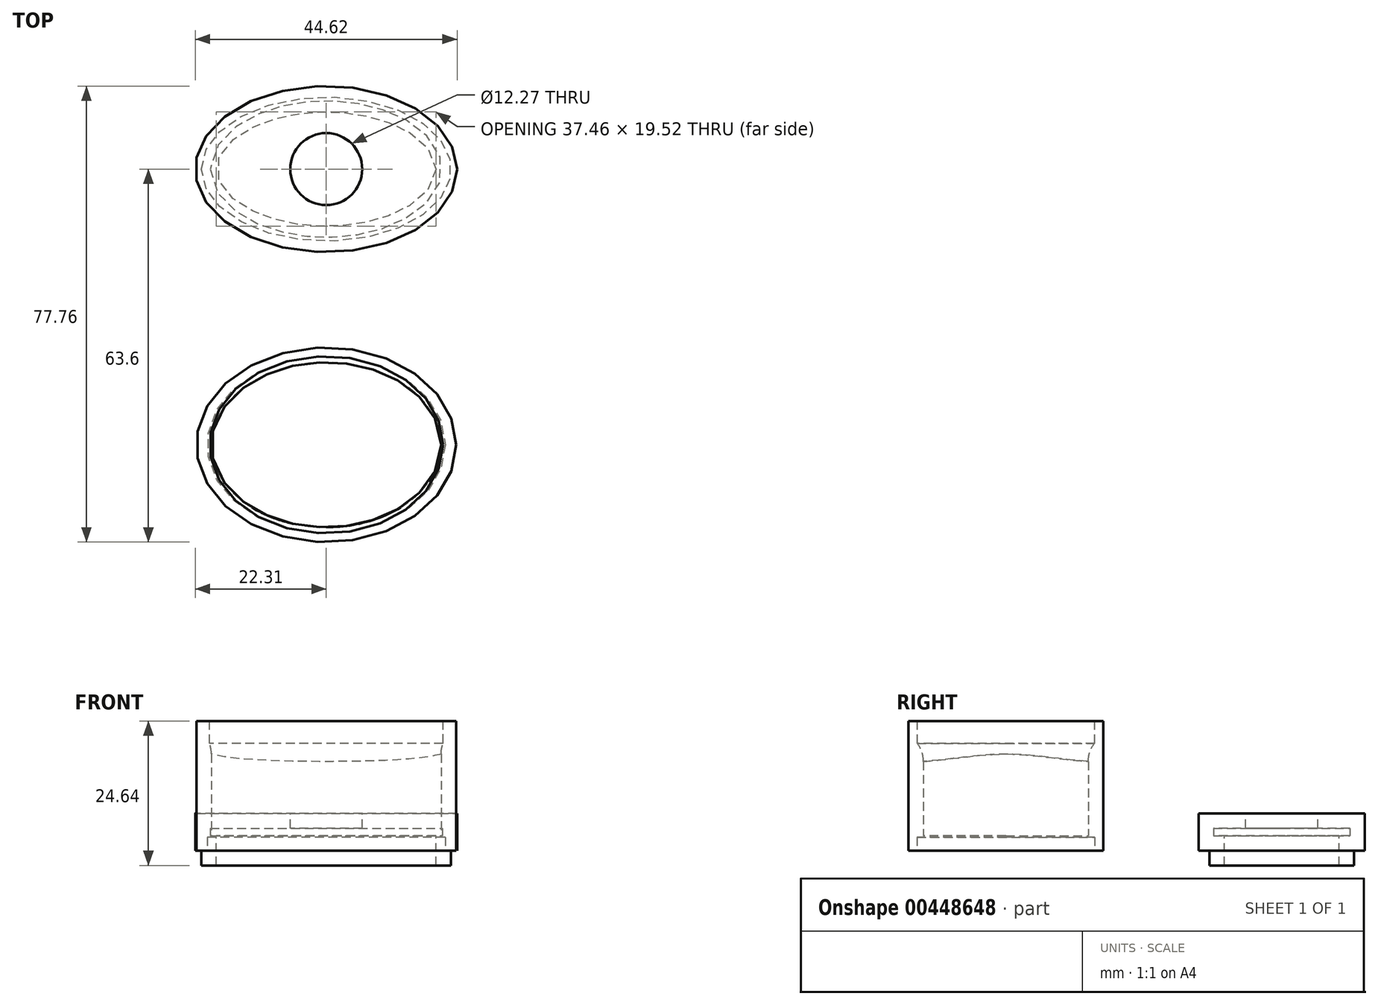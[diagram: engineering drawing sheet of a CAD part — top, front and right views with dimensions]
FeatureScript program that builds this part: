
annotation { "Feature Type Name" : "Feature", "Feature Type Description" : "" }
export const myFeature = defineFeature(function(context is Context, id is Id, definition is map)
    precondition{}
    {
        {
            var Q0;
            Q0=qCreatedBy(makeId("Top.planeOp"),FACE);
            var sketch = newSketch(context, id + "F0", { "sketchPlane" : qUnion([Q0])});
            skEllipse(sketch, "E0", {"center": v(0, 0) * mm, "majorRadius": 22.12 * mm, "minorRadius": 16.6 * mm, "majorAxis": v(1, 0)});
            skEllipse(sketch, "E1", {"center": v(0, 51.44) * mm, "majorRadius": 23.6 * mm, "minorRadius": 16.29 * mm, "majorAxis": v(1, 0)});
            skSolve(sketch);
        }
        {
            var Q0;
            Q0=makeQuery(id+"F0.imprint","IMPRINT",FACE,{"disambiguationData":[TD([[makeQuery(id+"F0.imprint","IMPRINT",EDGE,{"derivedFrom":sQuery(id+"F0.wireOp",EDGE,"E0")}),1.0]])]});
            extrude(context, id + "F1", {"entities" : qUnion([Q0]), "depth" : 22.1 * mm});
        }
        {
            var Q0;
            Q0=makeQuery(id+"F1.opExtrude","CAP_FACE",FACE,{"disambiguationData":[OSD([sQuery(id+"F0.wireOp",EDGE,"E0")])],"isStart":false});
            var sketch = newSketch(context, id + "F2", { "sketchPlane" : qUnion([Q0])});
            skEllipse(sketch, "E2", {"center": v(0, 0) * mm, "majorRadius": 19.92 * mm, "minorRadius": 15.11 * mm, "majorAxis": v(1, 0)});
            skSolve(sketch);
        }
        {
            var Q0;
            Q0 = qSketchRegion(id + "F2", true);
            extrude(context, id + "F3", {"entities" : qUnion([Q0]), "operationType" : NewBodyOperationType.REMOVE, "oppositeDirection" : true, "depth" : 3.8 * mm});
        }
        {
            var Q0;
            Q0=makeQuery(id+"F3.boolean.opBoolean","COPY",FACE,{"derivedFrom":makeQuery(id+"F3.opExtrude","CAP_FACE",FACE,{"disambiguationData":[OSD([sQuery(id+"F2.wireOp",EDGE,"E2")])],"isStart":false})});
            shell(context, id + "F4", {"entities" : qUnion([Q0]), "thickness" : 2.54 * mm});
        }
        {
            var Q0;
            Q0=makeQuery(id+"F3.boolean.opBoolean","COPY",EDGE,{"derivedFrom":makeQuery(id+"F3.opExtrude","CAP_EDGE",EDGE,{"disambiguationData":[OSD([sQuery(id+"F2.wireOp",EDGE,"E2")])],"isStart":true})});
            var Q1;
            Q1=makeQuery(id+"F4.opShell","TWEAK_EDGE",EDGE,{"derivedFrom":[makeQuery(id+"F1.opExtrude","SWEPT_FACE",FACE,{"disambiguationData":[OSD([sQuery(id+"F0.wireOp",EDGE,"E0")])]}),makeQuery(id+"F3.boolean.opBoolean","COPY",FACE,{"derivedFrom":makeQuery(id+"F3.opExtrude","CAP_FACE",FACE,{"disambiguationData":[OSD([sQuery(id+"F2.wireOp",EDGE,"E2")])],"isStart":false})})]});
            fillet(context, id + "F5", {"entities" : qUnion([Q0, Q1]), "radius" : 5.08 * mm, "tangentPropagation" : true, "allowEdgeOverflow" : false});
        }
        {
            var Q0;
            Q0=makeQuery(id+"F1.opExtrude","CAP_FACE",FACE,{"disambiguationData":[OSD([sQuery(id+"F0.wireOp",EDGE,"E0")])],"isStart":true});
            var sketch = newSketch(context, id + "F6", { "sketchPlane" : qUnion([Q0])});
            skEllipse(sketch, "E3", {"center": v(0, 0) * mm, "majorRadius": 20.28 * mm, "minorRadius": 15.13 * mm, "majorAxis": v(1, 0)});
            skSolve(sketch);
        }
        {
            var Q0;
            Q0 = qSketchRegion(id + "F6", true);
            extrude(context, id + "F7", {"entities" : qUnion([Q0]), "operationType" : NewBodyOperationType.REMOVE, "oppositeDirection" : true, "depth" : 2.3 * mm});
        }
        {
            var Q0;
            Q0=qCreatedBy(makeId("Top.planeOp"),FACE);
            var sketch = newSketch(context, id + "F8", { "sketchPlane" : qUnion([Q0])});
            skEllipse(sketch, "E4", {"center": v(0, 47.01) * mm, "majorRadius": 22.3 * mm, "minorRadius": 14.16 * mm, "majorAxis": v(1, 0)});
            skSolve(sketch);
        }
        {
            var Q0;
            Q0 = qSketchRegion(id + "F8", true);
            extrude(context, id + "F9", {"entities" : qUnion([Q0]), "depth" : 6.35 * mm});
        }
        {
            var Q0;
            Q0=makeQuery(id+"F9.opExtrude","CAP_FACE",FACE,{"disambiguationData":[OSD([sQuery(id+"F8.wireOp",EDGE,"E4")])],"isStart":true});
            var sketch = newSketch(context, id + "F10", { "sketchPlane" : qUnion([Q0])});
            skEllipse(sketch, "E5", {"center": v(0, -47.01) * mm, "majorRadius": 21.27 * mm, "minorRadius": 12.3 * mm, "majorAxis": v(-1, 0)});
            skSolve(sketch);
        }
        {
            var Q0;
            Q0 = qSketchRegion(id + "F10", true);
            extrude(context, id + "F11", {"entities" : qUnion([Q0]), "operationType" : NewBodyOperationType.ADD, "depth" : 2.54 * mm});
        }
        {
            var Q0;
            Q0=makeQuery(id+"F11.opExtrude","CAP_FACE",FACE,{"disambiguationData":[OSD([sQuery(id+"F10.wireOp",EDGE,"E5")])],"isStart":false});
            shell(context, id + "F12", {"entities" : qUnion([Q0]), "thickness" : 2.54 * mm});
        }
        {
            var Q0;
            Q0=makeQuery(id+"F9.opExtrude","CAP_FACE",FACE,{"disambiguationData":[OSD([sQuery(id+"F8.wireOp",EDGE,"E4")])],"isStart":false});
            var sketch = newSketch(context, id + "F13", { "sketchPlane" : qUnion([Q0])});
            skCircle(sketch, "E6", {"center": v(0, 47.01) * mm, "radius": 6.14 * mm});
            skSolve(sketch);
        }
        {
            var Q0;
            Q0 = qSketchRegion(id + "F13", true);
            extrude(context, id + "F14", {"entities" : qUnion([Q0]), "operationType" : NewBodyOperationType.REMOVE, "oppositeDirection" : true, "depth" : 25.4 * mm});
        }
    });
